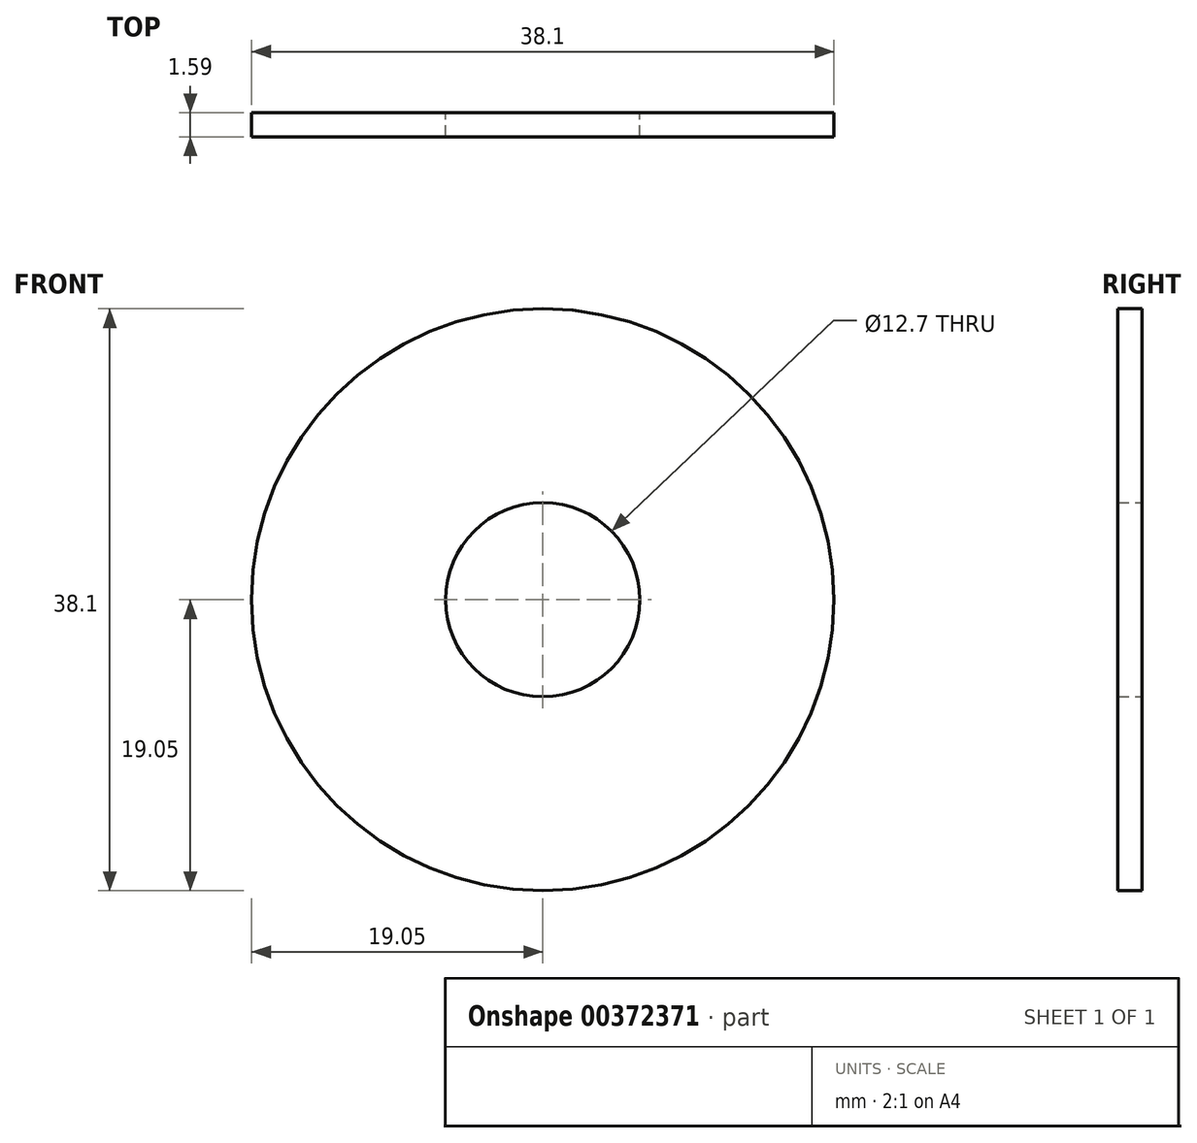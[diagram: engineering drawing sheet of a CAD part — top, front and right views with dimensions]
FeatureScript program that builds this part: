
annotation { "Feature Type Name" : "Feature", "Feature Type Description" : "" }
export const myFeature = defineFeature(function(context is Context, id is Id, definition is map)
    precondition{}
    {
        {
            var Q0;
            Q0=qCreatedBy(makeId("Front.planeOp"),FACE);
            var sketch = newSketch(context, id + "F0", { "sketchPlane" : qUnion([Q0])});
            skCircle(sketch, "E0", {"center": v(0, 0) * mm, "radius": 6.35 * mm});
            skCircle(sketch, "E1", {"center": v(0, 0) * mm, "radius": 19.05 * mm});
            skSolve(sketch);
        }
        {
            var Q0;
            Q0=makeQuery(id+"F0.imprint","IMPRINT",FACE,{"disambiguationData":[TD([[makeQuery(id+"F0.imprint","IMPRINT",EDGE,{"derivedFrom":sQuery(id+"F0.wireOp",EDGE,"E0")}),-1.0]])]});
            extrude(context, id + "F1", {"entities" : qUnion([Q0]), "depth" : 1.59 * mm});
        }
    });
